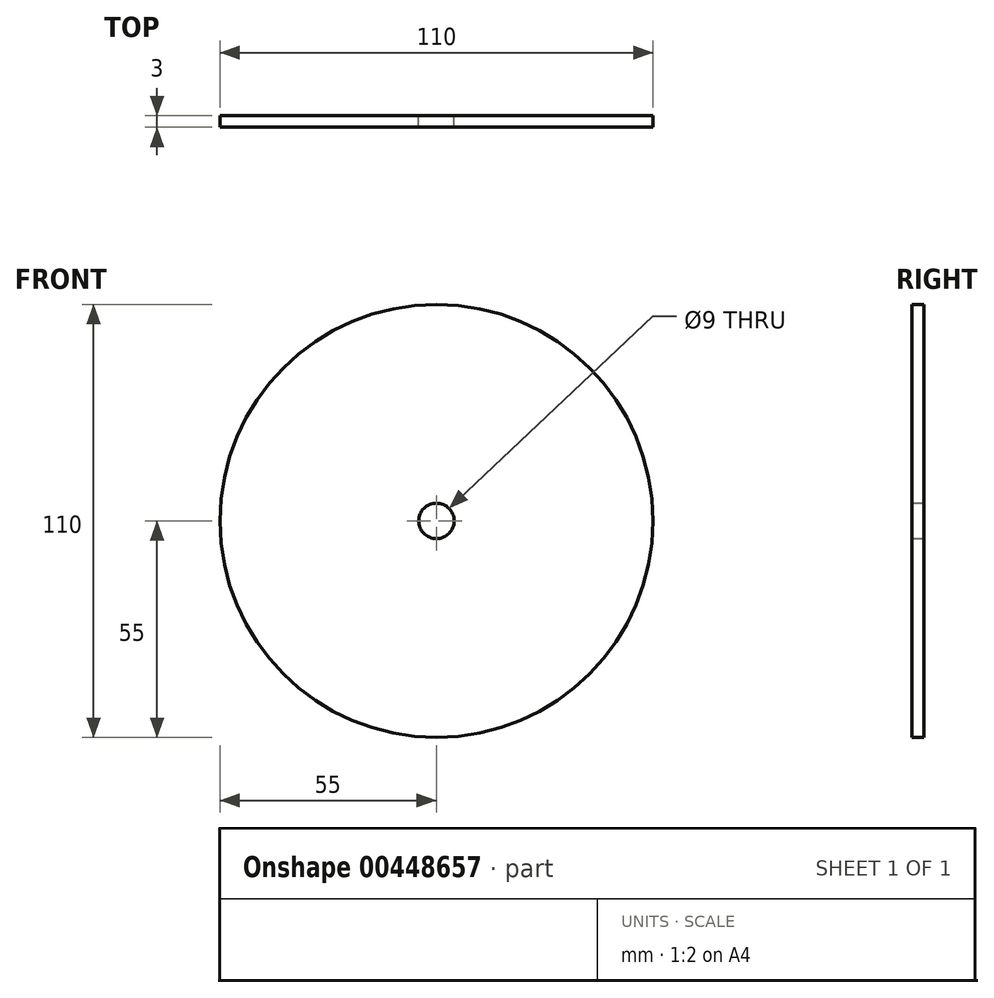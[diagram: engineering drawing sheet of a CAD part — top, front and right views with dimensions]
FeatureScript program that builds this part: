
annotation { "Feature Type Name" : "Feature", "Feature Type Description" : "" }
export const myFeature = defineFeature(function(context is Context, id is Id, definition is map)
    precondition{}
    {
        {
            var Q0;
            Q0=qCreatedBy(makeId("Front.planeOp"),FACE);
            var sketch = newSketch(context, id + "F0", { "sketchPlane" : qUnion([Q0])});
            skCircle(sketch, "E0", {"center": v(0, 0) * mm, "radius": 55 * mm});
            skCircle(sketch, "E1", {"center": v(0, 0) * mm, "radius": 4.5 * mm});
            skSolve(sketch);
        }
        {
            var Q0;
            Q0 = qSketchRegion(id + "F0", true);
            extrude(context, id + "F1", {"entities" : qUnion([Q0]), "depth" : 3 * mm});
        }
    });
